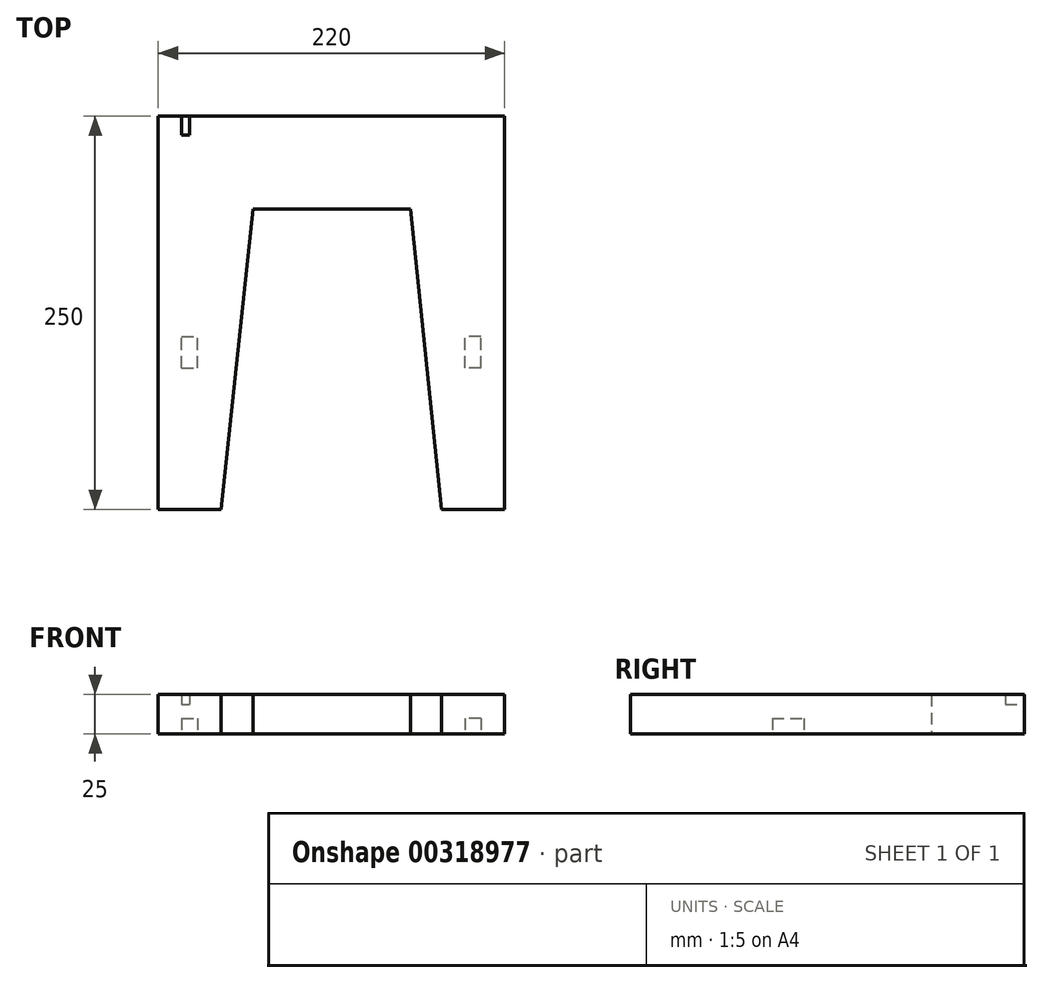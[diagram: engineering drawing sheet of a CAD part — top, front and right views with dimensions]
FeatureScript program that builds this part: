
annotation { "Feature Type Name" : "Feature", "Feature Type Description" : "" }
export const myFeature = defineFeature(function(context is Context, id is Id, definition is map)
    precondition{}
    {
        {
            var Q0;
            Q0=qCreatedBy(makeId("Top.planeOp"),FACE);
            var sketch = newSketch(context, id + "F0", { "sketchPlane" : qUnion([Q0])});
            skLineSegment(sketch, "E0.bottom", {"start": v(110, 125) * mm, "end": v(-110, 125) * mm});
            skLineSegment(sketch, "E0.left", {"start": v(110, 125) * mm, "end": v(110, -125) * mm});
            skLineSegment(sketch, "E0.right", {"start": v(-110, 125) * mm, "end": v(-110, -125) * mm});
            skPoint(sketch, "E0.middle", {"position": v(0, 0) * mm});
            skLineSegment(sketch, "E1", {"start": v(-110, -125) * mm, "end": v(-70, -125) * mm});
            skLineSegment(sketch, "E2", {"start": v(-70, -125) * mm, "end": v(-49.67, 66) * mm});
            skLineSegment(sketch, "E3", {"start": v(-49.67, 66) * mm, "end": v(50.33, 66) * mm});
            skLineSegment(sketch, "E4", {"start": v(50.33, 66) * mm, "end": v(70, -125) * mm});
            skLineSegment(sketch, "E5", {"start": v(70, -125) * mm, "end": v(110, -125) * mm});
            skPoint(sketch, "E6", {"position": v(0.33, 66) * mm});
            skSolve(sketch);
        }
        {
            var Q0;
            Q0=qSketchRegion(id+"F0",true);
            extrude(context, id + "F1", {"entities" : qUnion([Q0]), "depth" : 25 * mm});
        }
        {
            var Q0;
            Q0=makeQuery(id+"F1.opExtrude","SWEPT_FACE",FACE,{"disambiguationData":[OSD([sQuery(id+"F0.wireOp",EDGE,"E0.bottom")])]});
            var sketch = newSketch(context, id + "F2", { "sketchPlane" : qUnion([Q0])});
            skLineSegment(sketch, "E7", {"start": v(-110, 12.5) * mm, "end": v(110, 12.5) * mm, "construction": true});
            skPoint(sketch, "E8", {"position": v(-25, 12.5) * mm});
            skPoint(sketch, "E9", {"position": v(25, 12.5) * mm});
            skPoint(sketch, "E10", {"position": v(-95, 12.5) * mm});
            skPoint(sketch, "E11", {"position": v(95, 12.5) * mm});
            skLineSegment(sketch, "E12", {"start": v(-25, 12.5) * mm, "end": v(-25, 25) * mm, "construction": true});
            skLineSegment(sketch, "E13", {"start": v(25, 12.5) * mm, "end": v(25, 25) * mm, "construction": true});
            skLineSegment(sketch, "E14", {"start": v(95, 12.5) * mm, "end": v(95, 25) * mm, "construction": true});
            skLineSegment(sketch, "E15", {"start": v(-95, 12.5) * mm, "end": v(-95, 25) * mm, "construction": true});
            skPoint(sketch, "E16.middle", {"position": v(95, 25) * mm});
            skPoint(sketch, "E17.middle", {"position": v(25, 25) * mm});
            skPoint(sketch, "E18.middle", {"position": v(-25, 25) * mm});
            skPoint(sketch, "E19.middle", {"position": v(-95, 25) * mm});
            skPoint(sketch, "E20.oppositeSnap0", {"position": v(95, 18.75) * mm});
            skLineSegment(sketch, "E20.bottom", {"start": v(95, 25) * mm, "end": v(90.03, 25) * mm});
            skLineSegment(sketch, "E20.top", {"start": v(95, 18.75) * mm, "end": v(90.03, 18.75) * mm});
            skLineSegment(sketch, "E20.left", {"start": v(95, 25) * mm, "end": v(95, 18.75) * mm});
            skLineSegment(sketch, "E20.right", {"start": v(90.03, 25) * mm, "end": v(90.03, 18.75) * mm});
            skSolve(sketch);
        }
        {
            var Q0;
            Q0=qSketchRegion(id+"F2",true);
            extrude(context, id + "F3", {"entities" : qUnion([Q0]), "operationType" : NewBodyOperationType.REMOVE, "oppositeDirection" : true, "depth" : 12 * mm});
        }
        {
            var Q0;
            Q0=makeQuery(id+"F1.opExtrude","CAP_FACE",FACE,{"disambiguationData":[OSD([sQuery(id+"F0.wireOp",EDGE,"E0.bottom"),sQuery(id+"F0.wireOp",EDGE,"E0.left"),sQuery(id+"F0.wireOp",EDGE,"E0.right"),sQuery(id+"F0.wireOp",EDGE,"E1"),sQuery(id+"F0.wireOp",EDGE,"E2"),sQuery(id+"F0.wireOp",EDGE,"E3"),sQuery(id+"F0.wireOp",EDGE,"E4"),sQuery(id+"F0.wireOp",EDGE,"E5")])],"isStart":true});
            var sketch = newSketch(context, id + "F4", { "sketchPlane" : qUnion([Q0])});
            skLineSegment(sketch, "E21", {"start": v(-95, 125) * mm, "end": v(-95, 35) * mm, "construction": true});
            skLineSegment(sketch, "E22", {"start": v(-95, 35) * mm, "end": v(-110, 35) * mm, "construction": true});
            skLineSegment(sketch, "E23.bottom", {"start": v(-95, 35) * mm, "end": v(-85, 35) * mm});
            skLineSegment(sketch, "E23.top", {"start": v(-95, 15) * mm, "end": v(-85, 15) * mm});
            skLineSegment(sketch, "E23.left", {"start": v(-95, 35) * mm, "end": v(-95, 15) * mm});
            skLineSegment(sketch, "E23.right", {"start": v(-85, 35) * mm, "end": v(-85, 15) * mm});
            skLineSegment(sketch, "E24", {"start": v(0, 0) * mm, "end": v(0, 76.5) * mm});
            skLineSegment(sketch, "E25.MirrorCS", {"start": v(95, 35) * mm, "end": v(85, 35) * mm});
            skLineSegment(sketch, "E26.MirrorCS", {"start": v(95, 15) * mm, "end": v(85, 15) * mm});
            skLineSegment(sketch, "E27.MirrorCS", {"start": v(95, 35) * mm, "end": v(110, 35) * mm, "construction": true});
            skLineSegment(sketch, "E28.MirrorCS", {"start": v(95, 35) * mm, "end": v(95, 15) * mm});
            skLineSegment(sketch, "E29.MirrorCS", {"start": v(85, 35) * mm, "end": v(85, 15) * mm});
            skSolve(sketch);
        }
        {
            var Q0;
            Q0=qSketchRegion(id+"F4",true);
            extrude(context, id + "F5", {"entities" : qUnion([Q0]), "operationType" : NewBodyOperationType.REMOVE, "oppositeDirection" : true, "depth" : 10 * mm});
        }
    });
